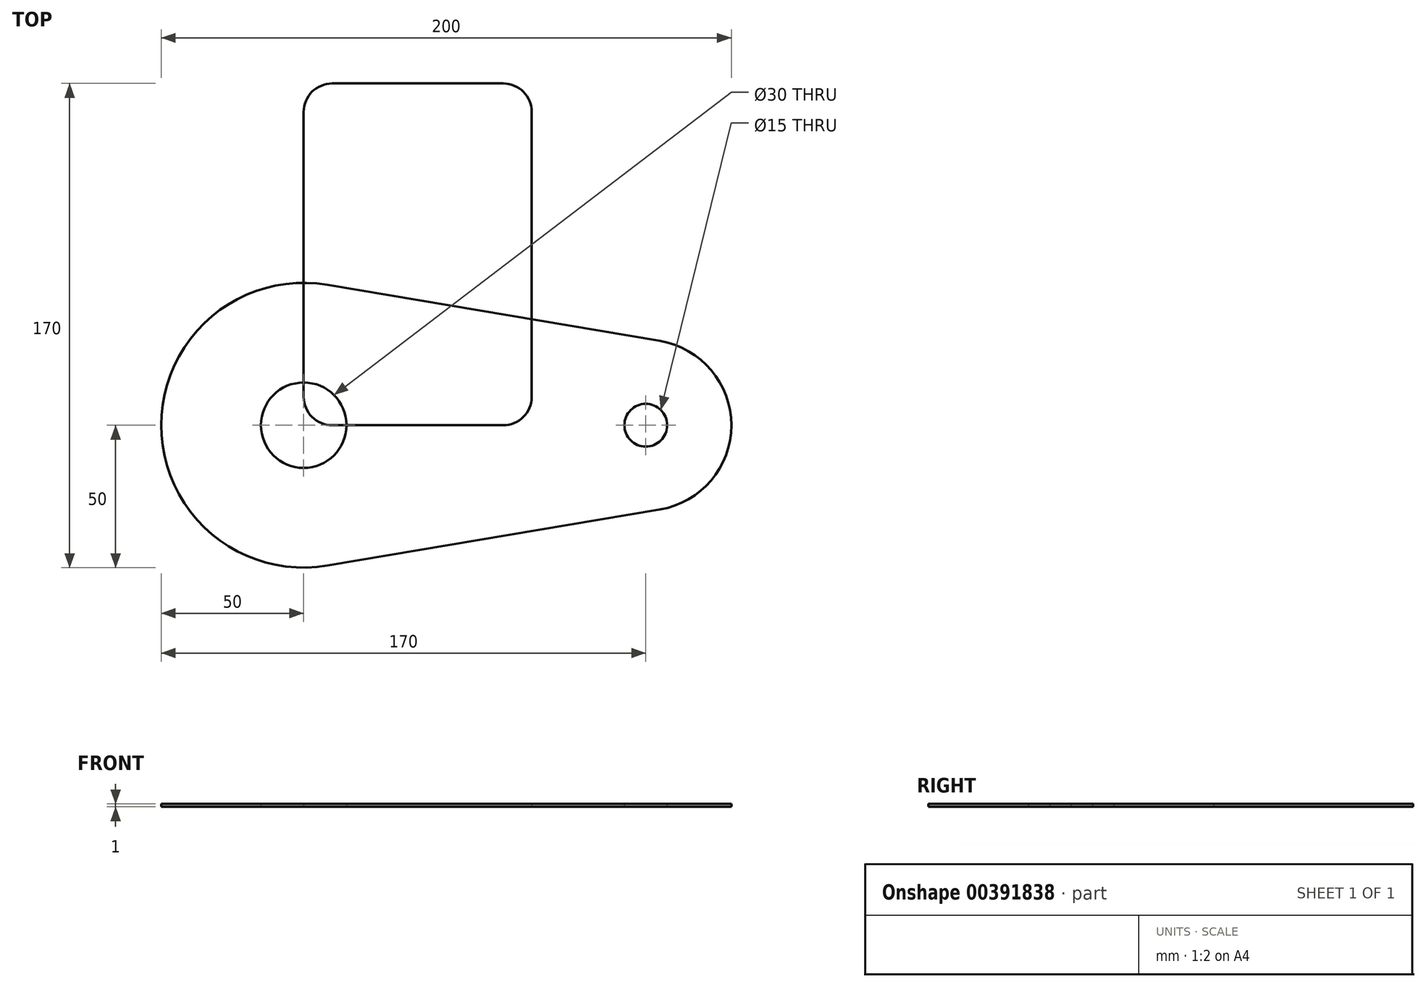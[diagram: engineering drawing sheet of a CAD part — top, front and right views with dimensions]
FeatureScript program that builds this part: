
annotation { "Feature Type Name" : "Feature", "Feature Type Description" : "" }
export const myFeature = defineFeature(function(context is Context, id is Id, definition is map)
    precondition{}
    {
        {
            var Q0;
            Q0=qCreatedBy(makeId("Top.planeOp"),FACE);
            var sketch = newSketch(context, id + "F0", { "sketchPlane" : qUnion([Q0])});
            skLineSegment(sketch, "E0.bottom", {"start": v(10, 0) * mm, "end": v(70, 0) * mm});
            skLineSegment(sketch, "E0.top", {"start": v(10, 120) * mm, "end": v(70, 120) * mm});
            skLineSegment(sketch, "E0.left", {"start": v(0, 10) * mm, "end": v(0, 110) * mm});
            skLineSegment(sketch, "E0.right", {"start": v(80, 10) * mm, "end": v(80, 110) * mm});
            skPoint(sketch, "E1.visualSharp", {"position": v(0, 120) * mm});
            skArc(sketch, "E1.filletArc", {"start": v(10, 120) * mm, "mid": v(2.93, 117.07) * mm, "end": v(0, 110) * mm});
            skPoint(sketch, "E2.visualSharp", {"position": v(80, 120) * mm});
            skArc(sketch, "E2.filletArc", {"start": v(80, 110) * mm, "mid": v(77.07, 117.07) * mm, "end": v(70, 120) * mm});
            skPoint(sketch, "E3.visualSharp", {"position": v(80, 0) * mm});
            skArc(sketch, "E3.filletArc", {"start": v(70, 0) * mm, "mid": v(77.07, 2.93) * mm, "end": v(80, 10) * mm});
            skPoint(sketch, "E4.visualSharp", {"position": v(0, 0) * mm});
            skArc(sketch, "E4.filletArc", {"start": v(0, 10) * mm, "mid": v(2.93, 2.93) * mm, "end": v(10, 0) * mm});
            skSolve(sketch);
        }
        {
            var Q0;
            Q0 = qSketchRegion(id + "F0", true);
            extrude(context, id + "F1", {"entities" : qUnion([Q0]), "depth" : 1 * mm});
        }
        {
            var Q0;
            Q0=qCreatedBy(makeId("Top.planeOp"),FACE);
            var sketch = newSketch(context, id + "F2", { "sketchPlane" : qUnion([Q0])});
            skArc(sketch, "E5", {"start": v(8.33, 49.3) * mm, "mid": v(-50, 0) * mm, "end": v(8.33, -49.3) * mm});
            skArc(sketch, "E6", {"start": v(125, -29.58) * mm, "mid": v(150, 0) * mm, "end": v(125, 29.58) * mm});
            skCircle(sketch, "E7", {"center": v(0, 0) * mm, "radius": 15 * mm});
            skCircle(sketch, "E8", {"center": v(120, 0) * mm, "radius": 7.5 * mm});
            skLineSegment(sketch, "E9", {"start": v(8.33, 49.3) * mm, "end": v(125, 29.58) * mm});
            skLineSegment(sketch, "E10", {"start": v(0, 0) * mm, "end": v(60.71, 0) * mm, "construction": true});
            skLineSegment(sketch, "E11.MirrorCS", {"start": v(8.33, -49.3) * mm, "end": v(125, -29.58) * mm});
            skSolve(sketch);
        }
        {
            var Q0;
            Q0 = qSketchRegion(id + "F2", true);
            extrude(context, id + "F3", {"entities" : qUnion([Q0]), "depth" : 1 * mm});
        }
    });
